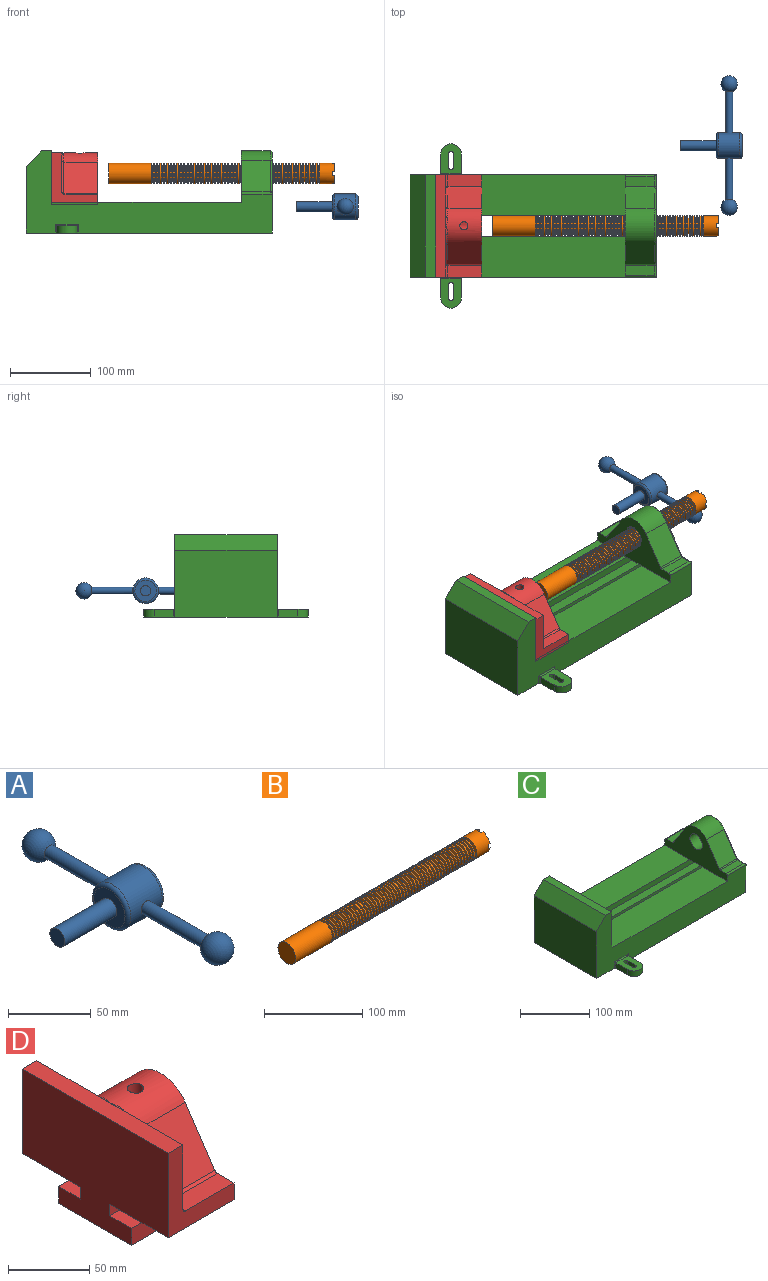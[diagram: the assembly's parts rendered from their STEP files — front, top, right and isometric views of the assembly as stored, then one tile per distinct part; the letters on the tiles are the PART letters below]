
ASSEMBLY  parts=4 mates=2
PART A: 11 faces, bbox 76.2x172.7x34.4 mm
  f0: sphere r=10.16mm, area 1231.8mm2, adj f1
  f1: cylinder r=4.45mm len=51.82mm, axis (0,1,0), area 1438.5mm2, adj f0,f4
  f2: sphere r=10.16mm, area 1231.8mm2, adj f3
  f3: cylinder r=4.45mm len=51.82mm, axis (0,1,0), area 1438.5mm2, adj f2,f4
  f4: cylinder r=15.88mm len=31.75mm, axis (-1,0,0), area 2534.7mm2, adj f1,f3,f9,f10
  f5: cylinder r=6.35mm len=44.45mm, axis (-1,0,0), area 1773.5mm2, adj f6,f8
  f6: plane 12.7x12.7mm, normal (-1,0,0), area 126.7mm2, adj f5
  f7: plane 26.67x26.67mm, normal (1,0,0), area 558.6mm2, adj f10
  f8: plane 26.67x26.67mm, normal (-1,0,0), area 432mm2, adj f5,f9
  f9: torus R=13.33mm, axis (1,0,0), area 374.8mm2, adj f4,f8
  f10: torus R=13.33mm, axis (1,0,0), area 374.8mm2, adj f4,f7
PART B: 220 faces, bbox 279.4x25.4x25.4 mm
  f0: cylinder r=12.7mm len=25.4mm, axis (-1,0,0), area 1468.2mm2, adj f1,f2,f3,f5,f7,f208,f209,f210
  f1: plane 9.9x9.9mm, normal (1,0,0), area 62.3mm2, adj f0,f4,f213,f216
  f2: plane 9.9x9.9mm, normal (1,0,0), area 62.3mm2, adj f0,f4,f210,f218
  f3: plane 9.9x9.9mm, normal (1,0,0), area 62.3mm2, adj f0,f4,f209,f212
  f4: cylinder r=6.35mm len=25.4mm, axis (1,0,0), area 960.3mm2, adj f1,f2,f3,f5,f6,f208,f209,f210
  f5: plane 9.9x9.9mm, normal (1,0,0), area 62.3mm2, adj f0,f4,f215,f217
  f6: plane 12.7x12.7mm, normal (1,0,0), area 126.7mm2, adj f4
  f7: cone r=12.7mm half-angle=76deg, axis (1,0,0), area 188mm2, adj f0,f9
  f8: cone r=10.16mm half-angle=76deg, axis (-1,0,0), area 188mm2, adj f9,f10
  f9: cylinder r=10.16mm len=20.32mm, axis (1,0,0), area 81.1mm2, adj f7,f8
  f10: cylinder r=12.7mm len=25.4mm, axis (-1,0,0), area 131.7mm2, adj f8,f11
  f11: cone r=12.7mm half-angle=76deg, axis (1,0,0), area 188mm2, adj f10,f13
  f12: cone r=10.16mm half-angle=76deg, axis (-1,0,0), area 188mm2, adj f13,f14
  f13: cylinder r=10.16mm len=20.32mm, axis (1,0,0), area 81.1mm2, adj f11,f12
  f14: cylinder r=12.7mm len=25.4mm, axis (-1,0,0), area 131.7mm2, adj f12,f15
  f15: cone r=12.7mm half-angle=76deg, axis (1,0,0), area 188mm2, adj f14,f17
  f16: cone r=10.16mm half-angle=76deg, axis (-1,0,0), area 188mm2, adj f17,f18
  f17: cylinder r=10.16mm len=20.32mm, axis (1,0,0), area 81.1mm2, adj f15,f16
  f18: cylinder r=12.7mm len=25.4mm, axis (-1,0,0), area 131.7mm2, adj f16,f19
  f19: cone r=12.7mm half-angle=76deg, axis (1,0,0), area 188mm2, adj f18,f21
  f20: cone r=10.16mm half-angle=76deg, axis (-1,0,0), area 188mm2, adj f21,f22
  f21: cylinder r=10.16mm len=20.32mm, axis (1,0,0), area 81.1mm2, adj f19,f20
  f22: cylinder r=12.7mm len=25.4mm, axis (-1,0,0), area 131.7mm2, adj f20,f23
  f23: cone r=12.7mm half-angle=76deg, axis (1,0,0), area 188mm2, adj f22,f25
  f24: cone r=10.16mm half-angle=76deg, axis (-1,0,0), area 188mm2, adj f25,f26
  f25: cylinder r=10.16mm len=20.32mm, axis (1,0,0), area 81.1mm2, adj f23,f24
  f26: cylinder r=12.7mm len=25.4mm, axis (-1,0,0), area 131.7mm2, adj f24,f27
  f27: cone r=12.7mm half-angle=76deg, axis (1,0,0), area 188mm2, adj f26,f29
  f28: cone r=10.16mm half-angle=76deg, axis (-1,0,0), area 188mm2, adj f29,f30
  f29: cylinder r=10.16mm len=20.32mm, axis (1,0,0), area 81.1mm2, adj f27,f28
  f30: cylinder r=12.7mm len=25.4mm, axis (-1,0,0), area 131.7mm2, adj f28,f31
  f31: cone r=12.7mm half-angle=76deg, axis (1,0,0), area 188mm2, adj f30,f33
  f32: cone r=10.16mm half-angle=76deg, axis (-1,0,0), area 188mm2, adj f33,f34
  f33: cylinder r=10.16mm len=20.32mm, axis (1,0,0), area 81.1mm2, adj f31,f32
  f34: cylinder r=12.7mm len=25.4mm, axis (-1,0,0), area 131.7mm2, adj f32,f35
  f35: cone r=12.7mm half-angle=76deg, axis (1,0,0), area 188mm2, adj f34,f37
  f36: cone r=10.16mm half-angle=76deg, axis (-1,0,0), area 188mm2, adj f37,f38
  f37: cylinder r=10.16mm len=20.32mm, axis (1,0,0), area 81.1mm2, adj f35,f36
  f38: cylinder r=12.7mm len=25.4mm, axis (-1,0,0), area 131.7mm2, adj f36,f39
  f39: cone r=12.7mm half-angle=76deg, axis (1,0,0), area 188mm2, adj f38,f41
  f40: cone r=10.16mm half-angle=76deg, axis (-1,0,0), area 188mm2, adj f41,f42
  f41: cylinder r=10.16mm len=20.32mm, axis (1,0,0), area 81.1mm2, adj f39,f40
  f42: cylinder r=12.7mm len=25.4mm, axis (-1,0,0), area 131.7mm2, adj f40,f43
  f43: cone r=12.7mm half-angle=76deg, axis (1,0,0), area 188mm2, adj f42,f45
  f44: cone r=10.16mm half-angle=76deg, axis (-1,0,0), area 188mm2, adj f45,f46
  f45: cylinder r=10.16mm len=20.32mm, axis (1,0,0), area 81.1mm2, adj f43,f44
  f46: cylinder r=12.7mm len=25.4mm, axis (-1,0,0), area 131.7mm2, adj f44,f47
  f47: cone r=12.7mm half-angle=76deg, axis (1,0,0), area 188mm2, adj f46,f49
  f48: cone r=10.16mm half-angle=76deg, axis (-1,0,0), area 188mm2, adj f49,f50
  f49: cylinder r=10.16mm len=20.32mm, axis (1,0,0), area 81.1mm2, adj f47,f48
  f50: cylinder r=12.7mm len=25.4mm, axis (-1,0,0), area 131.7mm2, adj f48,f51
  f51: cone r=12.7mm half-angle=76deg, axis (1,0,0), area 188mm2, adj f50,f53
  f52: cone r=10.16mm half-angle=76deg, axis (-1,0,0), area 188mm2, adj f53,f54
  f53: cylinder r=10.16mm len=20.32mm, axis (1,0,0), area 81.1mm2, adj f51,f52
  f54: cylinder r=12.7mm len=25.4mm, axis (-1,0,0), area 131.7mm2, adj f52,f55
  f55: cone r=12.7mm half-angle=76deg, axis (1,0,0), area 188mm2, adj f54,f57
  f56: cone r=10.16mm half-angle=76deg, axis (-1,0,0), area 188mm2, adj f57,f58
  f57: cylinder r=10.16mm len=20.32mm, axis (1,0,0), area 81.1mm2, adj f55,f56
  f58: cylinder r=12.7mm len=25.4mm, axis (-1,0,0), area 131.7mm2, adj f56,f59
  f59: cone r=12.7mm half-angle=76deg, axis (1,0,0), area 188mm2, adj f58,f61
  f60: cone r=10.16mm half-angle=76deg, axis (-1,0,0), area 188mm2, adj f61,f62
  f61: cylinder r=10.16mm len=20.32mm, axis (1,0,0), area 81.1mm2, adj f59,f60
  f62: cylinder r=12.7mm len=25.4mm, axis (-1,0,0), area 131.7mm2, adj f60,f63
  f63: cone r=12.7mm half-angle=76deg, axis (1,0,0), area 188mm2, adj f62,f65
  f64: cone r=10.16mm half-angle=76deg, axis (-1,0,0), area 188mm2, adj f65,f66
  f65: cylinder r=10.16mm len=20.32mm, axis (1,0,0), area 81.1mm2, adj f63,f64
  f66: cylinder r=12.7mm len=25.4mm, axis (-1,0,0), area 131.7mm2, adj f64,f67
  f67: cone r=12.7mm half-angle=76deg, axis (1,0,0), area 188mm2, adj f66,f69
  f68: cone r=10.16mm half-angle=76deg, axis (-1,0,0), area 188mm2, adj f69,f70
  f69: cylinder r=10.16mm len=20.32mm, axis (1,0,0), area 81.1mm2, adj f67,f68
  f70: cylinder r=12.7mm len=25.4mm, axis (-1,0,0), area 131.7mm2, adj f68,f71
  f71: cone r=12.7mm half-angle=76deg, axis (1,0,0), area 188mm2, adj f70,f73
  f72: cone r=10.16mm half-angle=76deg, axis (-1,0,0), area 188mm2, adj f73,f74
  f73: cylinder r=10.16mm len=20.32mm, axis (1,0,0), area 81.1mm2, adj f71,f72
  f74: cylinder r=12.7mm len=25.4mm, axis (-1,0,0), area 131.7mm2, adj f72,f75
  f75: cone r=12.7mm half-angle=76deg, axis (1,0,0), area 188mm2, adj f74,f77
  f76: cone r=10.16mm half-angle=76deg, axis (-1,0,0), area 188mm2, adj f77,f78
  f77: cylinder r=10.16mm len=20.32mm, axis (1,0,0), area 81.1mm2, adj f75,f76
  f78: cylinder r=12.7mm len=25.4mm, axis (-1,0,0), area 131.7mm2, adj f76,f79
  f79: cone r=12.7mm half-angle=76deg, axis (1,0,0), area 188mm2, adj f78,f81
  f80: cone r=10.16mm half-angle=76deg, axis (-1,0,0), area 188mm2, adj f81,f82
  f81: cylinder r=10.16mm len=20.32mm, axis (1,0,0), area 81.1mm2, adj f79,f80
  f82: cylinder r=12.7mm len=25.4mm, axis (-1,0,0), area 131.7mm2, adj f80,f83
  f83: cone r=12.7mm half-angle=76deg, axis (1,0,0), area 188mm2, adj f82,f85
  f84: cone r=10.16mm half-angle=76deg, axis (-1,0,0), area 188mm2, adj f85,f86
  f85: cylinder r=10.16mm len=20.32mm, axis (1,0,0), area 81.1mm2, adj f83,f84
  f86: cylinder r=12.7mm len=25.4mm, axis (-1,0,0), area 131.7mm2, adj f84,f87
  f87: cone r=12.7mm half-angle=76deg, axis (1,0,0), area 188mm2, adj f86,f89
  f88: cone r=10.16mm half-angle=76deg, axis (-1,0,0), area 188mm2, adj f89,f90
  f89: cylinder r=10.16mm len=20.32mm, axis (1,0,0), area 81.1mm2, adj f87,f88
  f90: cylinder r=12.7mm len=25.4mm, axis (-1,0,0), area 131.7mm2, adj f88,f91
  f91: cone r=12.7mm half-angle=76deg, axis (1,0,0), area 188mm2, adj f90,f93
  f92: cone r=10.16mm half-angle=76deg, axis (-1,0,0), area 188mm2, adj f93,f94
  f93: cylinder r=10.16mm len=20.32mm, axis (1,0,0), area 81.1mm2, adj f91,f92
  f94: cylinder r=12.7mm len=25.4mm, axis (-1,0,0), area 131.7mm2, adj f92,f95
  f95: cone r=12.7mm half-angle=76deg, axis (1,0,0), area 188mm2, adj f94,f97
  f96: cone r=10.16mm half-angle=76deg, axis (-1,0,0), area 188mm2, adj f97,f98
  f97: cylinder r=10.16mm len=20.32mm, axis (1,0,0), area 81.1mm2, adj f95,f96
  f98: cylinder r=12.7mm len=25.4mm, axis (-1,0,0), area 131.7mm2, adj f96,f99
  f99: cone r=12.7mm half-angle=76deg, axis (1,0,0), area 188mm2, adj f98,f101
  f100: cone r=10.16mm half-angle=76deg, axis (-1,0,0), area 188mm2, adj f101,f102
  f101: cylinder r=10.16mm len=20.32mm, axis (1,0,0), area 81.1mm2, adj f99,f100
  f102: cylinder r=12.7mm len=25.4mm, axis (-1,0,0), area 131.7mm2, adj f100,f103
  f103: cone r=12.7mm half-angle=76deg, axis (1,0,0), area 188mm2, adj f102,f105
  f104: cone r=10.16mm half-angle=76deg, axis (-1,0,0), area 188mm2, adj f105,f106
  f105: cylinder r=10.16mm len=20.32mm, axis (1,0,0), area 81.1mm2, adj f103,f104
  f106: cylinder r=12.7mm len=25.4mm, axis (-1,0,0), area 131.7mm2, adj f104,f107
  f107: cone r=12.7mm half-angle=76deg, axis (1,0,0), area 188mm2, adj f106,f109
  f108: cone r=10.16mm half-angle=76deg, axis (-1,0,0), area 188mm2, adj f109,f110
  f109: cylinder r=10.16mm len=20.32mm, axis (1,0,0), area 81.1mm2, adj f107,f108
  f110: cylinder r=12.7mm len=25.4mm, axis (-1,0,0), area 131.7mm2, adj f108,f111
  f111: cone r=12.7mm half-angle=76deg, axis (1,0,0), area 188mm2, adj f110,f113
  f112: cone r=10.16mm half-angle=76deg, axis (-1,0,0), area 188mm2, adj f113,f114
  f113: cylinder r=10.16mm len=20.32mm, axis (1,0,0), area 81.1mm2, adj f111,f112
  f114: cylinder r=12.7mm len=25.4mm, axis (-1,0,0), area 131.7mm2, adj f112,f115
  f115: cone r=12.7mm half-angle=76deg, axis (1,0,0), area 188mm2, adj f114,f117
  f116: cone r=10.16mm half-angle=76deg, axis (-1,0,0), area 188mm2, adj f117,f118
  f117: cylinder r=10.16mm len=20.32mm, axis (1,0,0), area 81.1mm2, adj f115,f116
  f118: cylinder r=12.7mm len=25.4mm, axis (-1,0,0), area 131.7mm2, adj f116,f119
  f119: cone r=12.7mm half-angle=76deg, axis (1,0,0), area 188mm2, adj f118,f121
  f120: cone r=10.16mm half-angle=76deg, axis (-1,0,0), area 188mm2, adj f121,f122
  f121: cylinder r=10.16mm len=20.32mm, axis (1,0,0), area 81.1mm2, adj f119,f120
  f122: cylinder r=12.7mm len=25.4mm, axis (-1,0,0), area 131.7mm2, adj f120,f123
  f123: cone r=12.7mm half-angle=76deg, axis (1,0,0), area 188mm2, adj f122,f125
  f124: cone r=10.16mm half-angle=76deg, axis (-1,0,0), area 188mm2, adj f125,f126
  f125: cylinder r=10.16mm len=20.32mm, axis (1,0,0), area 81.1mm2, adj f123,f124
  f126: cylinder r=12.7mm len=25.4mm, axis (-1,0,0), area 131.7mm2, adj f124,f127
  f127: cone r=12.7mm half-angle=76deg, axis (1,0,0), area 188mm2, adj f126,f129
  f128: cone r=10.16mm half-angle=76deg, axis (-1,0,0), area 188mm2, adj f129,f130
  f129: cylinder r=10.16mm len=20.32mm, axis (1,0,0), area 81.1mm2, adj f127,f128
  f130: cylinder r=12.7mm len=25.4mm, axis (-1,0,0), area 131.7mm2, adj f128,f131
  f131: cone r=12.7mm half-angle=76deg, axis (1,0,0), area 188mm2, adj f130,f133
  f132: cone r=10.16mm half-angle=76deg, axis (-1,0,0), area 188mm2, adj f133,f134
  f133: cylinder r=10.16mm len=20.32mm, axis (1,0,0), area 81.1mm2, adj f131,f132
  f134: cylinder r=12.7mm len=25.4mm, axis (-1,0,0), area 131.7mm2, adj f132,f135
  f135: cone r=12.7mm half-angle=76deg, axis (1,0,0), area 188mm2, adj f134,f137
  f136: cone r=10.16mm half-angle=76deg, axis (-1,0,0), area 188mm2, adj f137,f138
  f137: cylinder r=10.16mm len=20.32mm, axis (1,0,0), area 81.1mm2, adj f135,f136
  f138: cylinder r=12.7mm len=25.4mm, axis (-1,0,0), area 131.7mm2, adj f136,f139
  f139: cone r=12.7mm half-angle=76deg, axis (1,0,0), area 188mm2, adj f138,f141
  f140: cone r=10.16mm half-angle=76deg, axis (-1,0,0), area 188mm2, adj f141,f142
  f141: cylinder r=10.16mm len=20.32mm, axis (1,0,0), area 81.1mm2, adj f139,f140
  f142: cylinder r=12.7mm len=25.4mm, axis (-1,0,0), area 131.7mm2, adj f140,f143
  f143: cone r=12.7mm half-angle=76deg, axis (1,0,0), area 188mm2, adj f142,f145
  f144: cone r=10.16mm half-angle=76deg, axis (-1,0,0), area 188mm2, adj f145,f146
  f145: cylinder r=10.16mm len=20.32mm, axis (1,0,0), area 81.1mm2, adj f143,f144
  f146: cylinder r=12.7mm len=25.4mm, axis (-1,0,0), area 131.7mm2, adj f144,f147
  f147: cone r=12.7mm half-angle=76deg, axis (1,0,0), area 188mm2, adj f146,f149
  f148: cone r=10.16mm half-angle=76deg, axis (-1,0,0), area 188mm2, adj f149,f150
  f149: cylinder r=10.16mm len=20.32mm, axis (1,0,0), area 81.1mm2, adj f147,f148
  f150: cylinder r=12.7mm len=25.4mm, axis (-1,0,0), area 131.7mm2, adj f148,f151
  f151: cone r=12.7mm half-angle=76deg, axis (1,0,0), area 188mm2, adj f150,f153
  f152: cone r=10.16mm half-angle=76deg, axis (-1,0,0), area 188mm2, adj f153,f154
  f153: cylinder r=10.16mm len=20.32mm, axis (1,0,0), area 81.1mm2, adj f151,f152
  f154: cylinder r=12.7mm len=25.4mm, axis (-1,0,0), area 131.7mm2, adj f152,f155
  f155: cone r=12.7mm half-angle=76deg, axis (1,0,0), area 188mm2, adj f154,f157
  f156: cone r=10.16mm half-angle=76deg, axis (-1,0,0), area 188mm2, adj f157,f158
  f157: cylinder r=10.16mm len=20.32mm, axis (1,0,0), area 81.1mm2, adj f155,f156
  f158: cylinder r=12.7mm len=25.4mm, axis (-1,0,0), area 131.7mm2, adj f156,f159
  f159: cone r=12.7mm half-angle=76deg, axis (1,0,0), area 188mm2, adj f158,f161
  f160: cone r=10.16mm half-angle=76deg, axis (-1,0,0), area 188mm2, adj f161,f162
  f161: cylinder r=10.16mm len=20.32mm, axis (1,0,0), area 81.1mm2, adj f159,f160
  f162: cylinder r=12.7mm len=25.4mm, axis (-1,0,0), area 131.7mm2, adj f160,f163
  f163: cone r=12.7mm half-angle=76deg, axis (1,0,0), area 188mm2, adj f162,f165
  f164: cone r=10.16mm half-angle=76deg, axis (-1,0,0), area 188mm2, adj f165,f166
  f165: cylinder r=10.16mm len=20.32mm, axis (1,0,0), area 81.1mm2, adj f163,f164
  f166: cylinder r=12.7mm len=25.4mm, axis (-1,0,0), area 131.7mm2, adj f164,f167
  f167: cone r=12.7mm half-angle=76deg, axis (1,0,0), area 188mm2, adj f166,f169
  f168: cone r=10.16mm half-angle=76deg, axis (-1,0,0), area 188mm2, adj f169,f170
  f169: cylinder r=10.16mm len=20.32mm, axis (1,0,0), area 81.1mm2, adj f167,f168
  f170: cylinder r=12.7mm len=25.4mm, axis (-1,0,0), area 131.7mm2, adj f168,f171
  f171: cone r=12.7mm half-angle=76deg, axis (1,0,0), area 188mm2, adj f170,f173
  f172: cone r=10.16mm half-angle=76deg, axis (-1,0,0), area 188mm2, adj f173,f174
  f173: cylinder r=10.16mm len=20.32mm, axis (1,0,0), area 81.1mm2, adj f171,f172
  f174: cylinder r=12.7mm len=25.4mm, axis (-1,0,0), area 131.7mm2, adj f172,f175
  f175: cone r=12.7mm half-angle=76deg, axis (1,0,0), area 188mm2, adj f174,f177
  f176: cone r=10.16mm half-angle=76deg, axis (-1,0,0), area 188mm2, adj f177,f178
  f177: cylinder r=10.16mm len=20.32mm, axis (1,0,0), area 81.1mm2, adj f175,f176
  f178: cylinder r=12.7mm len=25.4mm, axis (-1,0,0), area 131.7mm2, adj f176,f179
  f179: cone r=12.7mm half-angle=76deg, axis (1,0,0), area 188mm2, adj f178,f181
  f180: cone r=10.16mm half-angle=76deg, axis (-1,0,0), area 188mm2, adj f181,f182
  f181: cylinder r=10.16mm len=20.32mm, axis (1,0,0), area 81.1mm2, adj f179,f180
  f182: cylinder r=12.7mm len=25.4mm, axis (-1,0,0), area 131.7mm2, adj f180,f183
  f183: cone r=12.7mm half-angle=76deg, axis (1,0,0), area 188mm2, adj f182,f185
  f184: cone r=10.16mm half-angle=76deg, axis (-1,0,0), area 188mm2, adj f185,f186
  f185: cylinder r=10.16mm len=20.32mm, axis (1,0,0), area 81.1mm2, adj f183,f184
  f186: cylinder r=12.7mm len=25.4mm, axis (-1,0,0), area 131.7mm2, adj f184,f187
  f187: cone r=12.7mm half-angle=76deg, axis (1,0,0), area 188mm2, adj f186,f189
  f188: cone r=10.16mm half-angle=76deg, axis (-1,0,0), area 188mm2, adj f189,f190
  f189: cylinder r=10.16mm len=20.32mm, axis (1,0,0), area 81.1mm2, adj f187,f188
  f190: cylinder r=12.7mm len=25.4mm, axis (-1,0,0), area 131.7mm2, adj f188,f191
  f191: cone r=12.7mm half-angle=76deg, axis (1,0,0), area 188mm2, adj f190,f193
  f192: cone r=10.16mm half-angle=76deg, axis (-1,0,0), area 188mm2, adj f193,f194
  f193: cylinder r=10.16mm len=20.32mm, axis (1,0,0), area 81.1mm2, adj f191,f192
  f194: cylinder r=12.7mm len=25.4mm, axis (-1,0,0), area 131.7mm2, adj f192,f195
  f195: cone r=12.7mm half-angle=76deg, axis (1,0,0), area 188mm2, adj f194,f197
  f196: cone r=10.16mm half-angle=76deg, axis (-1,0,0), area 188mm2, adj f197,f198
  f197: cylinder r=10.16mm len=20.32mm, axis (1,0,0), area 81.1mm2, adj f195,f196
  f198: cylinder r=12.7mm len=25.4mm, axis (-1,0,0), area 131.7mm2, adj f196,f199
  f199: cone r=12.7mm half-angle=76deg, axis (1,0,0), area 188mm2, adj f198,f201
  f200: cone r=10.16mm half-angle=76deg, axis (-1,0,0), area 188mm2, adj f201,f202
  f201: cylinder r=10.16mm len=20.32mm, axis (1,0,0), area 81.1mm2, adj f199,f200
  f202: cylinder r=12.7mm len=25.4mm, axis (-1,0,0), area 131.7mm2, adj f200,f203
  f203: cone r=12.7mm half-angle=76deg, axis (1,0,0), area 188mm2, adj f202,f205
  f204: cone r=10.16mm half-angle=76deg, axis (-1,0,0), area 188mm2, adj f205,f207
  f205: cylinder r=10.16mm len=20.32mm, axis (1,0,0), area 81.1mm2, adj f203,f204
  f206: plane 25.4x25.4mm, normal (-1,0,0), area 506.7mm2, adj f207
  f207: cylinder r=12.7mm len=52.45mm, axis (-1,0,0), area 4185.4mm2, adj f204,f206
  f208: plane 6.88x5.08mm, normal (1,0,0), area 32.7mm2, adj f0,f4,f209,f210
  f209: plane 6.62x2.54mm, normal (0,-1,0), area 16.8mm2, adj f0,f3,f4,f208
  f210: plane 6.62x2.54mm, normal (0,1,0), area 16.8mm2, adj f0,f2,f4,f208
  f211: plane 6.88x5.08mm, normal (1,0,0), area 32.7mm2, adj f0,f4,f212,f213
  f212: plane 6.62x2.54mm, normal (0,0,1), area 16.8mm2, adj f0,f3,f4,f211
  f213: plane 6.62x2.54mm, normal (0,0,-1), area 16.8mm2, adj f0,f1,f4,f211
  f214: plane 6.88x5.08mm, normal (1,0,0), area 32.7mm2, adj f0,f4,f215,f216
  f215: plane 6.62x2.54mm, normal (0,1,0), area 16.8mm2, adj f0,f4,f5,f214
  f216: plane 6.62x2.54mm, normal (0,-1,0), area 16.8mm2, adj f0,f1,f4,f214
  f217: plane 6.62x2.54mm, normal (0,0,-1), area 16.8mm2, adj f0,f4,f5,f219
  f218: plane 6.62x2.54mm, normal (0,0,1), area 16.8mm2, adj f0,f2,f4,f219
  f219: plane 6.88x5.08mm, normal (1,0,0), area 32.7mm2, adj f0,f4,f217,f218
PART C: 61 faces, bbox 304.8x203.2x103.7 mm
  f0: plane 304.8x101.6mm, normal (0,1,0), area 13520.3mm2, adj f3,f4,f5,f6,f7,f8,f9,f16
  f1: plane 304.8x101.6mm, normal (0,-1,0), area 13520.3mm2, adj f2,f3,f5,f6,f7,f8,f9,f16
  f2: plane 234.95x50.8mm, normal (0,0,1), area 11935.5mm2, adj f1,f5,f16,f26
  f3: plane 127x99.06mm, normal (1,0,0), area 7097.5mm2, adj f0,f1,f9,f14,f17,f18,f19,f20
  f4: plane 234.95x50.8mm, normal (0,0,1), area 11935.5mm2, adj f0,f5,f16,f27
  f5: plane 127x101.6mm, normal (1,0,0), area 9516.1mm2, adj f0,f1,f2,f4,f6,f9,f18,f19
  f6: plane 127x12.7mm, normal (0,0,1), area 1612.9mm2, adj f0,f1,f5,f7
  f7: plane 127x19.05mm, normal (-0.71,0,0.71), area 3421.5mm2, adj f0,f1,f6,f8
  f8: plane 127x82.55mm, normal (-1,0,0), area 10483.8mm2, adj f0,f1,f7,f9
  f9: plane 304.8x203.2mm, normal (0,0,-1), area 33298.3mm2, adj f0,f1,f3,f5,f8,f21,f22,f39
  f10: plane 35.56x11.98mm, normal (0,0,1), area 426mm2, adj f16,f28,f29,f30
  f11: plane 38.43x35.56mm, normal (0,0.83,0.56), area 1645.4mm2, adj f12,f16,f29,f32
  f12: cylinder r=25.4mm len=42.19mm, axis (1,0,0), area 1770.2mm2, adj f11,f13,f16,f33
  f13: plane 38.43x35.56mm, normal (0,-0.83,0.56), area 1645.4mm2, adj f12,f16,f34,f35
  f14: cylinder r=12.7mm len=38.1mm, axis (1,0,0), area 3040.2mm2, adj f3,f16
  f15: plane 35.56x11.98mm, normal (0,0,1), area 426mm2, adj f16,f34,f36,f38
  f16: plane 127x63.5mm, normal (-1,0,0), area 4155.5mm2, adj f0,f1,f2,f4,f10,f11,f12,f13
  f17: plane 38.1x25.4mm, normal (0,0,-1), area 967.7mm2, adj f3,f16,f26,f27
  f18: plane 273.05x19.05mm, normal (0,0,-1), area 5201.6mm2, adj f3,f5,f19,f26
  f19: plane 273.05x12.7mm, normal (0,1,0), area 3467.7mm2, adj f3,f5,f18,f20
  f20: plane 273.05x19.05mm, normal (0,0,1), area 5201.6mm2, adj f3,f5,f19,f21
  f21: plane 273.05x16.51mm, normal (0,1,0), area 4508.1mm2, adj f3,f5,f9,f20
  f22: plane 273.05x16.51mm, normal (0,-1,0), area 4508.1mm2, adj f3,f5,f9,f23
  f23: plane 273.05x19.05mm, normal (0,0,1), area 5201.6mm2, adj f3,f5,f22,f24
  f24: plane 273.05x12.7mm, normal (0,-1,0), area 3467.7mm2, adj f3,f5,f23,f25
  f25: plane 273.05x19.05mm, normal (0,0,-1), area 5201.6mm2, adj f3,f5,f24,f27
  f26: plane 273.05x8.89mm, normal (0,1,0), area 2427.4mm2, adj f2,f3,f5,f17,f18
  f27: plane 273.05x8.89mm, normal (0,-1,0), area 2427.4mm2, adj f3,f4,f5,f17,f25
  f28: cylinder r=2.54mm len=38.1mm, axis (1,0,0), area 148.3mm2, adj f0,f10,f16,f30
  f29: cylinder r=2.54mm len=35.56mm, axis (-1,0,0), area 88.5mm2, adj f10,f11,f16,f31
  f30: cylinder r=2.54mm len=14.52mm, axis (0,1,0), area 54.3mm2, adj f3,f10,f28,f31
  f31: torus R=5.08mm, axis (-1,0,0), area 13.5mm2, adj f3,f29,f30,f32
  f32: cylinder r=2.54mm len=39.84mm, axis (0,0.56,-0.83), area 184.6mm2, adj f3,f11,f31,f33
  f33: torus R=22.86mm, axis (-1,0,0), area 191.4mm2, adj f3,f12,f32,f35
  f34: cylinder r=2.54mm len=35.56mm, axis (-1,0,0), area 88.5mm2, adj f13,f15,f16,f37
  f35: cylinder r=2.54mm len=39.84mm, axis (0,0.56,0.83), area 184.6mm2, adj f3,f13,f33,f37
  f36: cylinder r=2.54mm len=38.1mm, axis (-1,0,0), area 148.3mm2, adj f1,f15,f16,f38
  f37: torus R=5.08mm, axis (-1,0,0), area 13.5mm2, adj f3,f34,f35,f38
  f38: cylinder r=2.54mm len=14.52mm, axis (0,1,0), area 54.3mm2, adj f3,f15,f36,f37
  f39: plane 23.88x9.53mm, normal (-1,0,0), area 227.4mm2, adj f9,f45,f46,f60
  f40: plane 23.88x9.53mm, normal (1,0,0), area 227.4mm2, adj f9,f45,f46,f58
  f41: cylinder r=3.3mm len=9.53mm, axis (0,0,-1), area 98.8mm2, adj f9,f42,f44,f46
  f42: plane 15.62x9.53mm, normal (-1,0,0), area 148.8mm2, adj f9,f41,f43,f46
  f43: cylinder r=3.3mm len=9.53mm, axis (0,0,-1), area 98.8mm2, adj f9,f42,f44,f46
  f44: plane 15.62x9.53mm, normal (1,0,0), area 148.8mm2, adj f9,f41,f43,f46
  f45: cylinder r=12.7mm len=25.4mm, axis (0,0,-1), area 380mm2, adj f9,f39,f40,f46
  f46: plane 36.58x25.4mm, normal (0,0,1), area 722.4mm2, adj f39,f40,f41,f42,f43,f44,f45,f59
  f47: plane 23.88x9.53mm, normal (-1,0,0), area 227.4mm2, adj f9,f53,f54,f56
  f48: plane 23.88x9.53mm, normal (1,0,0), area 227.4mm2, adj f9,f53,f54,f55
  f49: cylinder r=3.3mm len=9.53mm, axis (0,0,-1), area 98.8mm2, adj f9,f50,f52,f54
  f50: plane 15.62x9.53mm, normal (-1,0,0), area 148.8mm2, adj f9,f49,f51,f54
  f51: cylinder r=3.3mm len=9.53mm, axis (0,0,-1), area 98.8mm2, adj f9,f50,f52,f54
  f52: plane 15.62x9.53mm, normal (1,0,0), area 148.8mm2, adj f9,f49,f51,f54
  f53: cylinder r=12.7mm len=25.4mm, axis (0,0,-1), area 380mm2, adj f9,f47,f48,f54
  f54: plane 36.58x25.4mm, normal (0,0,1), area 722.4mm2, adj f47,f48,f49,f50,f51,f52,f53,f57
  f55: cylinder r=1.52mm len=11.05mm, axis (0,0,-1), area 24.1mm2, adj f0,f9,f48,f57
  f56: cylinder r=1.52mm len=11.05mm, axis (0,0,1), area 24.1mm2, adj f0,f9,f47,f57
  f57: cylinder r=1.52mm len=28.45mm, axis (1,0,0), area 63.5mm2, adj f0,f54,f55,f56
  f58: cylinder r=1.52mm len=11.05mm, axis (0,0,1), area 24.1mm2, adj f1,f9,f40,f59
  f59: cylinder r=1.52mm len=28.45mm, axis (-1,0,0), area 63.5mm2, adj f1,f46,f58,f60
  f60: cylinder r=1.52mm len=11.05mm, axis (0,0,-1), area 24.1mm2, adj f1,f9,f39,f59
PART D: 36 faces, bbox 57.2x127x89 mm
  f0: plane 57.15x50.8mm, normal (0,0,-1), area 2903.2mm2, adj f6,f9,f10,f23
  f1: cylinder r=12.7mm len=44.45mm, axis (1,0,0), area 3464.3mm2, adj f6,f15,f16
  f2: plane 41.91x14.52mm, normal (0,0,1), area 608.5mm2, adj f6,f11,f24,f25
  f3: plane 51.86x48.26mm, normal (1,0,0), area 1495.7mm2, adj f8,f10,f31,f33,f35
  f4: plane 51.86x48.26mm, normal (1,0,0), area 1495.7mm2, adj f8,f11,f24,f28,f29
  f5: plane 57.15x50.8mm, normal (0,0,-1), area 2903.2mm2, adj f6,f9,f11,f22
  f6: plane 127x85.09mm, normal (1,0,0), area 5190.6mm2, adj f0,f1,f2,f5,f7,f10,f11,f12
  f7: plane 41.91x14.52mm, normal (0,0,1), area 608.5mm2, adj f6,f10,f30,f31
  f8: plane 127x12.7mm, normal (0,0,1), area 1612.9mm2, adj f3,f4,f9,f10,f11,f26,f34
  f9: plane 127x85.09mm, normal (-1,0,0), area 9096.8mm2, adj f0,f5,f8,f10,f11,f17,f18,f19
  f10: plane 63.5x57.15mm, normal (0,-1,0), area 1372.3mm2, adj f0,f3,f6,f7,f8,f9,f31
  f11: plane 63.5x57.15mm, normal (0,1,0), area 1372.3mm2, adj f2,f4,f5,f6,f8,f9,f24
  f12: plane 41.91x38.43mm, normal (0,-0.83,0.56), area 1939.2mm2, adj f6,f13,f30,f33
  f13: cylinder r=25.4mm len=44.45mm, axis (1,0,0), area 2026.5mm2, adj f6,f12,f14,f16,f26,f28,f34,f35
  f14: plane 41.91x38.43mm, normal (0,0.83,0.56), area 1939.2mm2, adj f6,f13,f25,f29
  f15: plane 25.4x25.4mm, normal (1,0,0), area 506.7mm2, adj f1
  f16: cylinder r=5.08mm len=13.76mm, axis (0,0,1), area 414mm2, adj f1,f13
  f17: plane 57.15x19.05mm, normal (0,0,1), area 1088.7mm2, adj f6,f9,f18,f23
  f18: plane 57.15x12.7mm, normal (0,-1,0), area 725.8mm2, adj f6,f9,f17,f19
  f19: plane 63.5x57.15mm, normal (0,0,-1), area 3629mm2, adj f6,f9,f18,f20
  f20: plane 57.15x12.7mm, normal (0,1,0), area 725.8mm2, adj f6,f9,f19,f21
  f21: plane 57.15x19.05mm, normal (0,0,1), area 1088.7mm2, adj f6,f9,f20,f22
  f22: plane 57.15x8.89mm, normal (0,1,0), area 508.1mm2, adj f5,f6,f9,f21
  f23: plane 57.15x8.89mm, normal (0,-1,0), area 508.1mm2, adj f0,f6,f9,f17
  f24: cylinder r=2.54mm len=14.52mm, axis (0,-1,0), area 57.9mm2, adj f2,f4,f11,f27
  f25: cylinder r=2.54mm len=41.91mm, axis (1,0,0), area 104.3mm2, adj f2,f6,f14,f27
  f26: bspline ~12.24x2.8mm, area 20.9mm2, adj f8,f13,f28
  f27: sphere r=2.54mm, area 6.3mm2, adj f24,f25,f29
  f28: torus R=27.94mm, axis (1,0,0), area 57.8mm2, adj f4,f13,f26,f29
  f29: cylinder r=2.54mm len=39.84mm, axis (0,-0.56,0.83), area 184.6mm2, adj f4,f14,f27,f28
  f30: cylinder r=2.54mm len=41.91mm, axis (1,0,0), area 104.3mm2, adj f6,f7,f12,f32
  f31: cylinder r=2.54mm len=14.52mm, axis (0,-1,0), area 57.9mm2, adj f3,f7,f10,f32
  f32: sphere r=2.54mm, area 6.3mm2, adj f30,f31,f33
  f33: cylinder r=2.54mm len=39.84mm, axis (0,-0.56,-0.83), area 184.6mm2, adj f3,f12,f32,f35
  f34: bspline ~12.24x2.8mm, area 20.9mm2, adj f8,f13,f35
  f35: torus R=27.94mm, axis (1,0,0), area 57.8mm2, adj f3,f13,f33,f34
PLACE A t=(-308.75,6.44,265.82)mm
PLACE B t=(-287.07,-93,307.03)mm
PLACE C t=(-345.04,-93,309.52)mm
PLACE D t=(-345.04,-93,307.03)mm
MATE slider B.f7 <-> D.f28  axis (1,0,0) through (-478.21,-93,383.23)mm
MATE fastened C.f5 <-> D.f9  axis (1,0,0) through (-618.09,-93,371.82)mm
